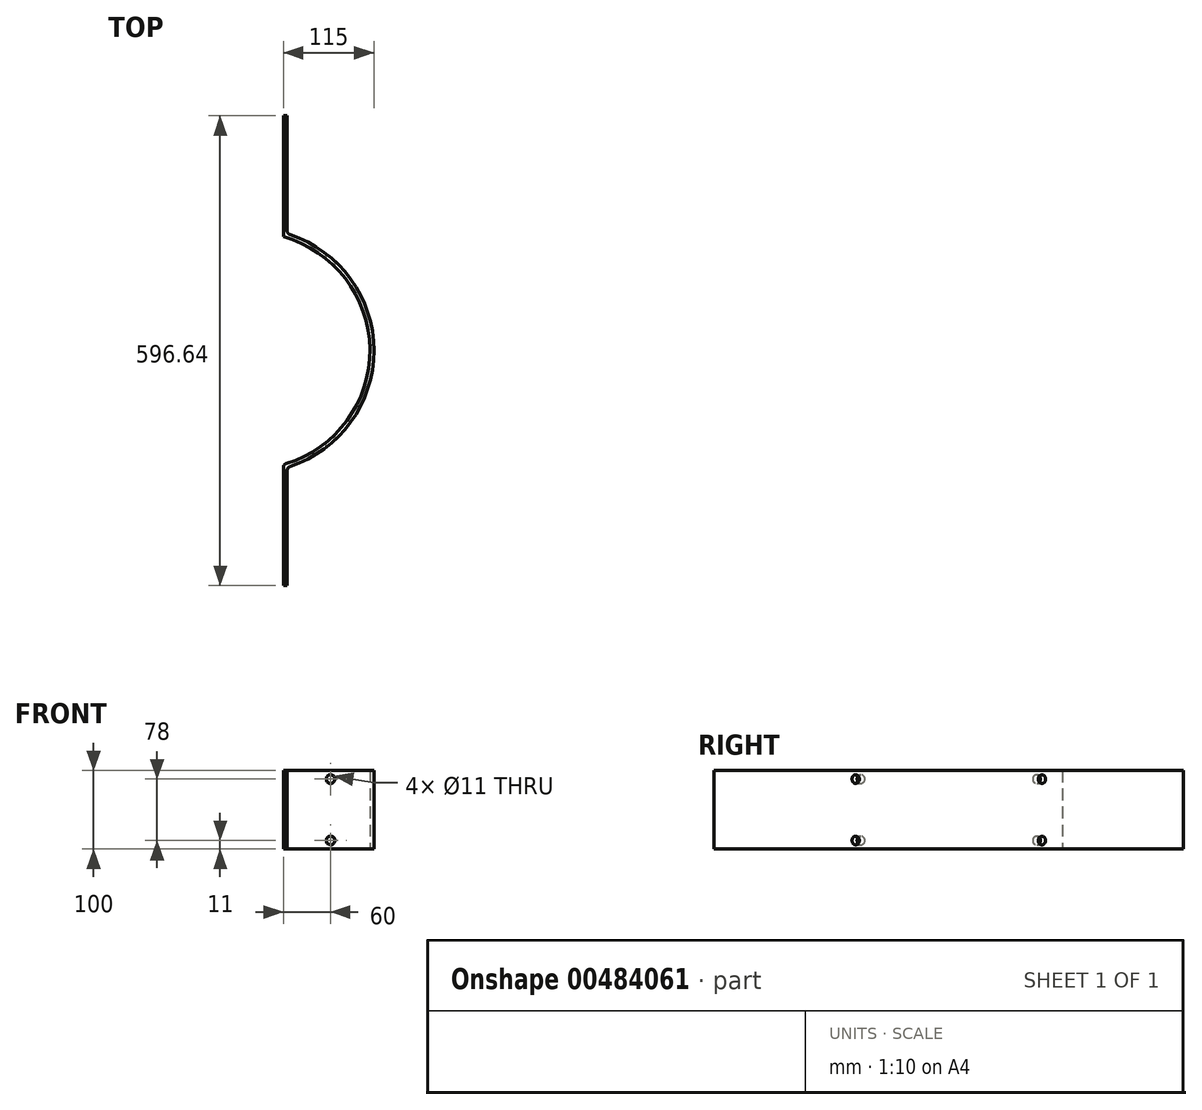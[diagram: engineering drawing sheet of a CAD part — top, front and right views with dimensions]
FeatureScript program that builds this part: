
annotation { "Feature Type Name" : "Feature", "Feature Type Description" : "" }
export const myFeature = defineFeature(function(context is Context, id is Id, definition is map)
    precondition{}
    {
        {
            var Q0;
            Q0=qCreatedBy(makeId("Top.planeOp"),FACE);
            var sketch = newSketch(context, id + "F0", { "sketchPlane" : qUnion([Q0])});
            skLineSegment(sketch, "E0", {"start": v(45, -151.99) * mm, "end": v(45, -298.32) * mm});
            skLineSegment(sketch, "E1", {"start": v(45, 151.99) * mm, "end": v(45, 298.32) * mm});
            skLineSegment(sketch, "E2", {"start": v(45, 298.32) * mm, "end": v(40, 298.32) * mm});
            skLineSegment(sketch, "E3", {"start": v(40, -298.32) * mm, "end": v(45, -298.32) * mm});
            skLineSegment(sketch, "E4", {"start": v(40, 144.57) * mm, "end": v(40, 298.32) * mm});
            skArc(sketch, "E5", {"start": v(43.54, -143.54) * mm, "mid": v(149.89, 1.85) * mm, "end": v(40, 144.57) * mm});
            skArc(sketch, "E6", {"start": v(48.44, -147.24) * mm, "mid": v(155, 0) * mm, "end": v(48.44, 147.24) * mm});
            skLineSegment(sketch, "E7", {"start": v(40, -148.32) * mm, "end": v(40, -298.32) * mm});
            skPoint(sketch, "E8.visualSharp", {"position": v(45, 148.32) * mm});
            skArc(sketch, "E8.filletArc", {"start": v(45, 151.99) * mm, "mid": v(45.95, 149.06) * mm, "end": v(48.44, 147.24) * mm});
            skPoint(sketch, "E9.visualSharp", {"position": v(45, -148.32) * mm});
            skArc(sketch, "E9.filletArc", {"start": v(48.44, -147.24) * mm, "mid": v(45.95, -149.06) * mm, "end": v(45, -151.99) * mm});
            skPoint(sketch, "E10.visualSharp", {"position": v(40, -144.57) * mm});
            skArc(sketch, "E10.filletArc", {"start": v(43.54, -143.54) * mm, "mid": v(40.98, -145.34) * mm, "end": v(40, -148.32) * mm});
            skSolve(sketch);
        }
        {
            var Q0;
            Q0 = qSketchRegion(id + "F0", true);
            extrude(context, id + "F1", {"entities" : qUnion([Q0]), "depth" : 100 * mm});
        }
        {
            var Q0;
            Q0=makeQuery(id+"F1.opExtrude","SWEPT_FACE",FACE,{"disambiguationData":[OSD([sQuery(id+"F0.wireOp",EDGE,"E3")])]});
            var sketch = newSketch(context, id + "F2", { "sketchPlane" : qUnion([Q0])});
            skLineSegment(sketch, "E11", {"start": v(45, 0) * mm, "end": v(45, 100) * mm});
            skLineSegment(sketch, "E12", {"start": v(45, 50) * mm, "end": v(100, 50) * mm});
            skLineSegment(sketch, "E13", {"start": v(100, 50) * mm, "end": v(100, 89) * mm});
            skLineSegment(sketch, "E14", {"start": v(100, 50) * mm, "end": v(100, 11) * mm});
            skSolve(sketch);
        }
        {
            var Q0;
            Q0=sQuery(id+"F2.wireOp",VERTEX,"E13.end");
            var Q1;
            Q1=sQuery(id+"F2.wireOp",VERTEX,"E14.end");
            var Q2;
            Q2=makeQuery(id+"F1.opExtrude","SWEPT_BODY",BODY,{"disambiguationData":[OSD([sQuery(id+"F0.wireOp",EDGE,"E0"),sQuery(id+"F0.wireOp",EDGE,"E1"),sQuery(id+"F0.wireOp",EDGE,"E2"),sQuery(id+"F0.wireOp",EDGE,"E3"),sQuery(id+"F0.wireOp",EDGE,"E5"),sQuery(id+"F0.wireOp",EDGE,"E6"),sQuery(id+"F0.wireOp",EDGE,"E7"),sQuery(id+"F0.wireOp",EDGE,"E4"),sQuery(id+"F0.wireOp",EDGE,"E8.filletArc"),sQuery(id+"F0.wireOp",EDGE,"E9.filletArc"),sQuery(id+"F0.wireOp",EDGE,"E10.filletArc")])]});
            hole(context, id + "F3", {"style" : HoleStyle.SIMPLE, "endStyle" : HoleEndStyle.THROUGH, "standardTappedOrClearance" : lookupTablePath({ "standard" : "ISO", "fit" : "Normal", "size" : "M10", "type" : "Clearance" }), "standardBlindInLast" : lookupTablePath({ "fit" : "Standard", "standard" : "ISO", "size" : "M10", "type" : "Clearance" }), "holeDiameter" : 11 * mm, "isTappedThrough" : true, "tappedDepth" : 12 * mm, "tapClearance" : 3, "locations" : qUnion([Q0, Q1]), "scope" : qUnion([Q2])});
        }
    });
